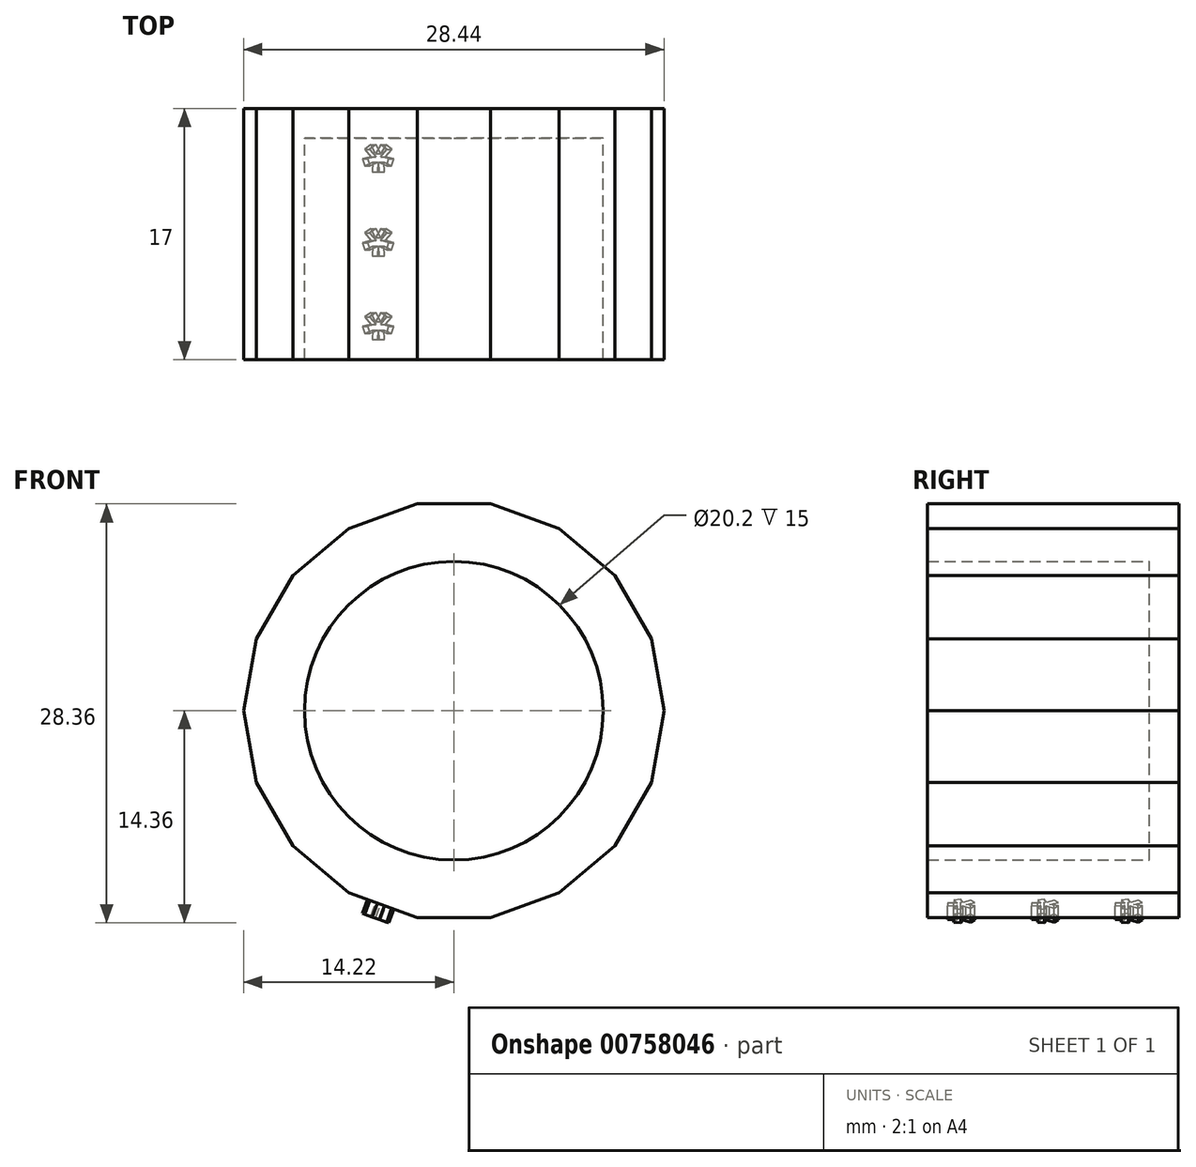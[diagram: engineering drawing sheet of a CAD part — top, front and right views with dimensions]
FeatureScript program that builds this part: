
annotation { "Feature Type Name" : "Feature", "Feature Type Description" : "" }
export const myFeature = defineFeature(function(context is Context, id is Id, definition is map)
    precondition{}
    {
        {
            var Q0;
            Q0=qCreatedBy(makeId("Front.planeOp"),FACE);
            var sketch = newSketch(context, id + "F0", { "sketchPlane" : qUnion([Q0])});
            skCircle(sketch, "E0", {"center": v(0, 0) * mm, "radius": 10.05 * mm});
            skCircle(sketch, "E1.cCircle", {"center": v(0, 0) * mm, "radius": 14 * mm, "construction": true});
            skLineSegment(sketch, "E1.0", {"start": v(-2.47, 14) * mm, "end": v(2.47, 14) * mm});
            skLineSegment(sketch, "E1.1", {"start": v(2.47, 14) * mm, "end": v(7.1, 12.31) * mm});
            skLineSegment(sketch, "E1.2", {"start": v(7.1, 12.31) * mm, "end": v(10.9, 9.14) * mm});
            skLineSegment(sketch, "E1.3", {"start": v(10.9, 9.14) * mm, "end": v(13.36, 4.86) * mm});
            skLineSegment(sketch, "E1.4", {"start": v(13.36, 4.86) * mm, "end": v(14.22, 0) * mm});
            skLineSegment(sketch, "E1.5", {"start": v(14.22, 0) * mm, "end": v(13.36, -4.86) * mm});
            skLineSegment(sketch, "E1.6", {"start": v(13.36, -4.86) * mm, "end": v(10.9, -9.14) * mm});
            skLineSegment(sketch, "E1.7", {"start": v(10.9, -9.14) * mm, "end": v(7.1, -12.31) * mm});
            skLineSegment(sketch, "E1.8", {"start": v(7.1, -12.31) * mm, "end": v(2.47, -14) * mm});
            skLineSegment(sketch, "E1.9", {"start": v(2.47, -14) * mm, "end": v(-2.47, -14) * mm});
            skLineSegment(sketch, "E1.10", {"start": v(-2.47, -14) * mm, "end": v(-7.1, -12.31) * mm});
            skLineSegment(sketch, "E1.11", {"start": v(-7.1, -12.31) * mm, "end": v(-10.9, -9.14) * mm});
            skLineSegment(sketch, "E1.12", {"start": v(-10.9, -9.14) * mm, "end": v(-13.36, -4.86) * mm});
            skLineSegment(sketch, "E1.13", {"start": v(-13.36, -4.86) * mm, "end": v(-14.22, 0) * mm});
            skLineSegment(sketch, "E1.14", {"start": v(-14.22, 0) * mm, "end": v(-13.36, 4.86) * mm});
            skLineSegment(sketch, "E1.15", {"start": v(-13.36, 4.86) * mm, "end": v(-10.9, 9.14) * mm});
            skLineSegment(sketch, "E1.16", {"start": v(-10.9, 9.14) * mm, "end": v(-7.1, 12.31) * mm});
            skLineSegment(sketch, "E1.17", {"start": v(-7.1, 12.31) * mm, "end": v(-2.47, 14) * mm});
            skPoint(sketch, "E1.0.midPoint", {"position": v(0, 14) * mm});
            skSolve(sketch);
        }
        {
            var Q0;
            Q0 = qSketchRegion(id + "F0", true);
            var Q1;
            Q1=makeQuery(id+"F0.imprint","IMPRINT",FACE,{"disambiguationData":[TD([[makeQuery(id+"F0.imprint","IMPRINT",EDGE,{"derivedFrom":sQuery(id+"F0.wireOp",EDGE,"E0")}),1.0]])]});
            extrude(context, id + "F1", {"entities" : qUnion([Q0, Q1]), "depth" : 2 * mm, "offsetDistance" : 25 * mm});
        }
        {
            var Q0;
            Q0=makeQuery(id+"F1.opExtrude","CAP_FACE",FACE,{"disambiguationData":[OSD([sQuery(id+"F0.wireOp",EDGE,"E1.0"),sQuery(id+"F0.wireOp",EDGE,"E1.1"),sQuery(id+"F0.wireOp",EDGE,"E1.2"),sQuery(id+"F0.wireOp",EDGE,"E1.3"),sQuery(id+"F0.wireOp",EDGE,"E1.4"),sQuery(id+"F0.wireOp",EDGE,"E1.5"),sQuery(id+"F0.wireOp",EDGE,"E1.6"),sQuery(id+"F0.wireOp",EDGE,"E1.7"),sQuery(id+"F0.wireOp",EDGE,"E1.8"),sQuery(id+"F0.wireOp",EDGE,"E1.9"),sQuery(id+"F0.wireOp",EDGE,"E1.10"),sQuery(id+"F0.wireOp",EDGE,"E1.11"),sQuery(id+"F0.wireOp",EDGE,"E1.12"),sQuery(id+"F0.wireOp",EDGE,"E1.13"),sQuery(id+"F0.wireOp",EDGE,"E1.14"),sQuery(id+"F0.wireOp",EDGE,"E1.15"),sQuery(id+"F0.wireOp",EDGE,"E1.16"),sQuery(id+"F0.wireOp",EDGE,"E1.17")])],"isStart":false});
            var sketch = newSketch(context, id + "F2", { "sketchPlane" : qUnion([Q0])});
            skCircle(sketch, "E2.cCircle", {"center": v(0, 0) * mm, "radius": 14 * mm, "construction": true});
            skLineSegment(sketch, "E2.0", {"start": v(-2.47, 14) * mm, "end": v(2.47, 14) * mm});
            skLineSegment(sketch, "E2.1", {"start": v(2.47, 14) * mm, "end": v(7.1, 12.31) * mm});
            skLineSegment(sketch, "E2.2", {"start": v(7.1, 12.31) * mm, "end": v(10.9, 9.14) * mm});
            skLineSegment(sketch, "E2.3", {"start": v(10.9, 9.14) * mm, "end": v(13.36, 4.86) * mm});
            skLineSegment(sketch, "E2.4", {"start": v(13.36, 4.86) * mm, "end": v(14.22, 0) * mm});
            skLineSegment(sketch, "E2.5", {"start": v(14.22, 0) * mm, "end": v(13.36, -4.86) * mm});
            skLineSegment(sketch, "E2.6", {"start": v(13.36, -4.86) * mm, "end": v(10.9, -9.14) * mm});
            skLineSegment(sketch, "E2.7", {"start": v(10.9, -9.14) * mm, "end": v(7.1, -12.31) * mm});
            skLineSegment(sketch, "E2.8", {"start": v(7.1, -12.31) * mm, "end": v(2.47, -14) * mm});
            skLineSegment(sketch, "E2.9", {"start": v(2.47, -14) * mm, "end": v(-2.47, -14) * mm});
            skLineSegment(sketch, "E2.10", {"start": v(-2.47, -14) * mm, "end": v(-7.1, -12.31) * mm});
            skLineSegment(sketch, "E2.11", {"start": v(-7.1, -12.31) * mm, "end": v(-10.9, -9.14) * mm});
            skLineSegment(sketch, "E2.12", {"start": v(-10.9, -9.14) * mm, "end": v(-13.36, -4.86) * mm});
            skLineSegment(sketch, "E2.13", {"start": v(-13.36, -4.86) * mm, "end": v(-14.22, 0) * mm});
            skLineSegment(sketch, "E2.14", {"start": v(-14.22, 0) * mm, "end": v(-13.36, 4.86) * mm});
            skLineSegment(sketch, "E2.15", {"start": v(-13.36, 4.86) * mm, "end": v(-10.9, 9.14) * mm});
            skLineSegment(sketch, "E2.16", {"start": v(-10.9, 9.14) * mm, "end": v(-7.1, 12.31) * mm});
            skLineSegment(sketch, "E2.17", {"start": v(-7.1, 12.31) * mm, "end": v(-2.47, 14) * mm});
            skPoint(sketch, "E2.0.midPoint", {"position": v(0, 14) * mm});
            skCircle(sketch, "E3", {"center": v(0, 0) * mm, "radius": 10.1 * mm});
            skSolve(sketch);
        }
        {
            var Q0;
            Q0 = qSketchRegion(id + "F2", true);
            extrude(context, id + "F3", {"entities" : qUnion([Q0]), "operationType" : NewBodyOperationType.ADD, "depth" : 15 * mm, "offsetDistance" : 25 * mm});
        }
        {
            var Q0;
            Q0=makeQuery(id+"F3.boolean.opBoolean","MERGE",FACE,{"derivedFrom":[makeQuery(id+"F1.opExtrude","SWEPT_FACE",FACE,{"disambiguationData":[OSD([sQuery(id+"F0.wireOp",EDGE,"E1.10")])]}),makeQuery(id+"F3.opExtrude","SWEPT_FACE",FACE,{"disambiguationData":[OSD([sQuery(id+"F2.wireOp",EDGE,"E2.10")])]})]});
            var sketch = newSketch(context, id + "F4", { "sketchPlane" : qUnion([Q0])});
            skText(sketch, "E4", { "text": "*\n*\n*", "fontName": "Arimo-Bold.ttf"});
            const initialGuessF4  = {"E4": [-0.00113, 0.01225, 1, 0, 0.00355]};
            skSetInitialGuess(sketch, initialGuessF4);
            skSolve(sketch);
        }
        {
            var Q0;
            Q0 = qSketchRegion(id + "F4", true);
            extrude(context, id + "F5", {"entities" : qUnion([Q0]), "operationType" : NewBodyOperationType.ADD, "depth" : 1 * mm, "offsetDistance" : 25 * mm});
        }
    });
